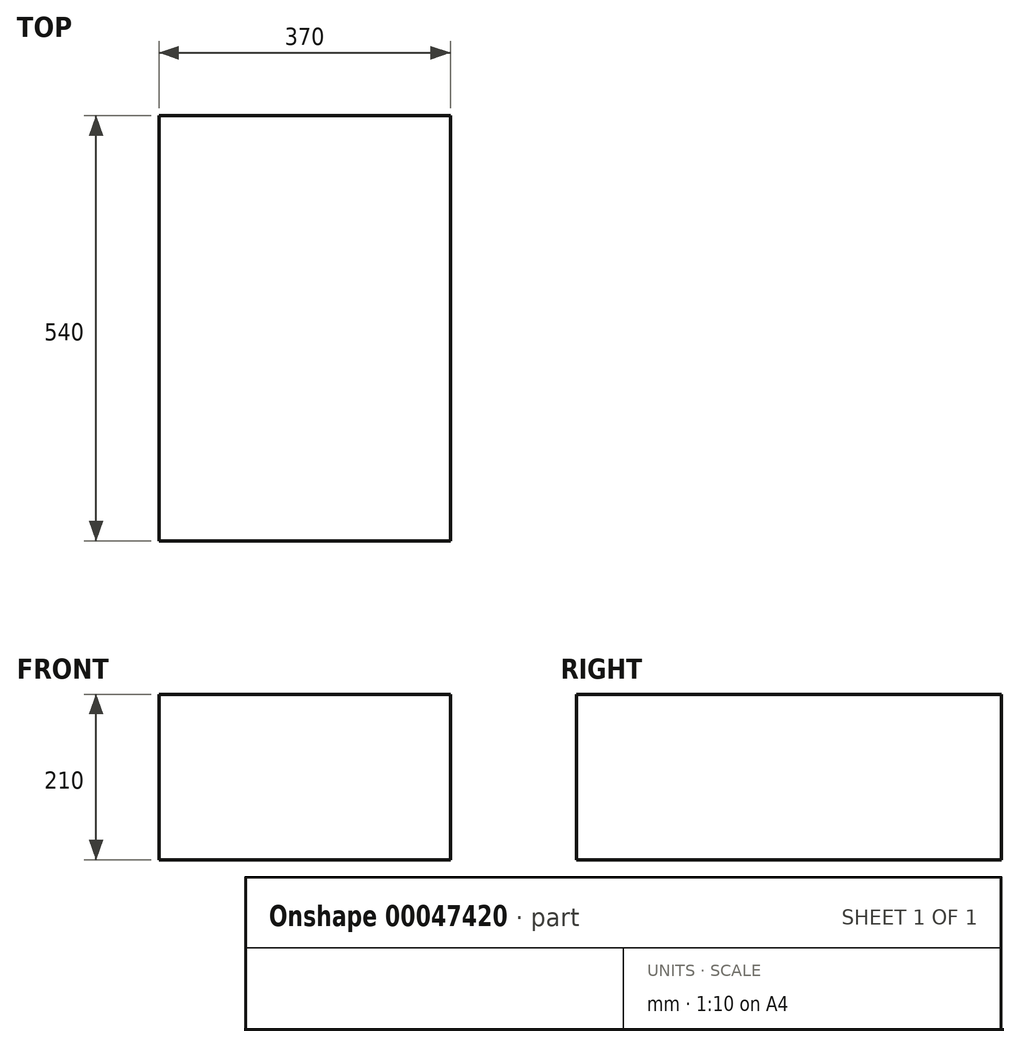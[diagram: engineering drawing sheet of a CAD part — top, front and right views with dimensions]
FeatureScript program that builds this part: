
annotation { "Feature Type Name" : "Feature", "Feature Type Description" : "" }
export const myFeature = defineFeature(function(context is Context, id is Id, definition is map)
    precondition{}
    {
        {
            var Q0;
            Q0=qCreatedBy(makeId("Top.planeOp"),FACE);
            var sketch = newSketch(context, id + "F0", { "sketchPlane" : qUnion([Q0])});
            skLineSegment(sketch, "E0.rect.bottom", {"start": v(185, 270) * mm, "end": v(-185, 270) * mm});
            skLineSegment(sketch, "E0.rect.top", {"start": v(185, -270) * mm, "end": v(-185, -270) * mm});
            skLineSegment(sketch, "E0.rect.left", {"start": v(185, 270) * mm, "end": v(185, -270) * mm});
            skLineSegment(sketch, "E0.rect.right", {"start": v(-185, 270) * mm, "end": v(-185, -270) * mm});
            skPoint(sketch, "E0.rect.middle", {"position": v(0, 0) * mm});
            skSolve(sketch);
        }
        {
            var Q0;
            Q0 = qSketchRegion(id + "F0", true);
            extrude(context, id + "F1", {"entities" : qUnion([Q0]), "depth" : 210 * mm});
        }
    });
